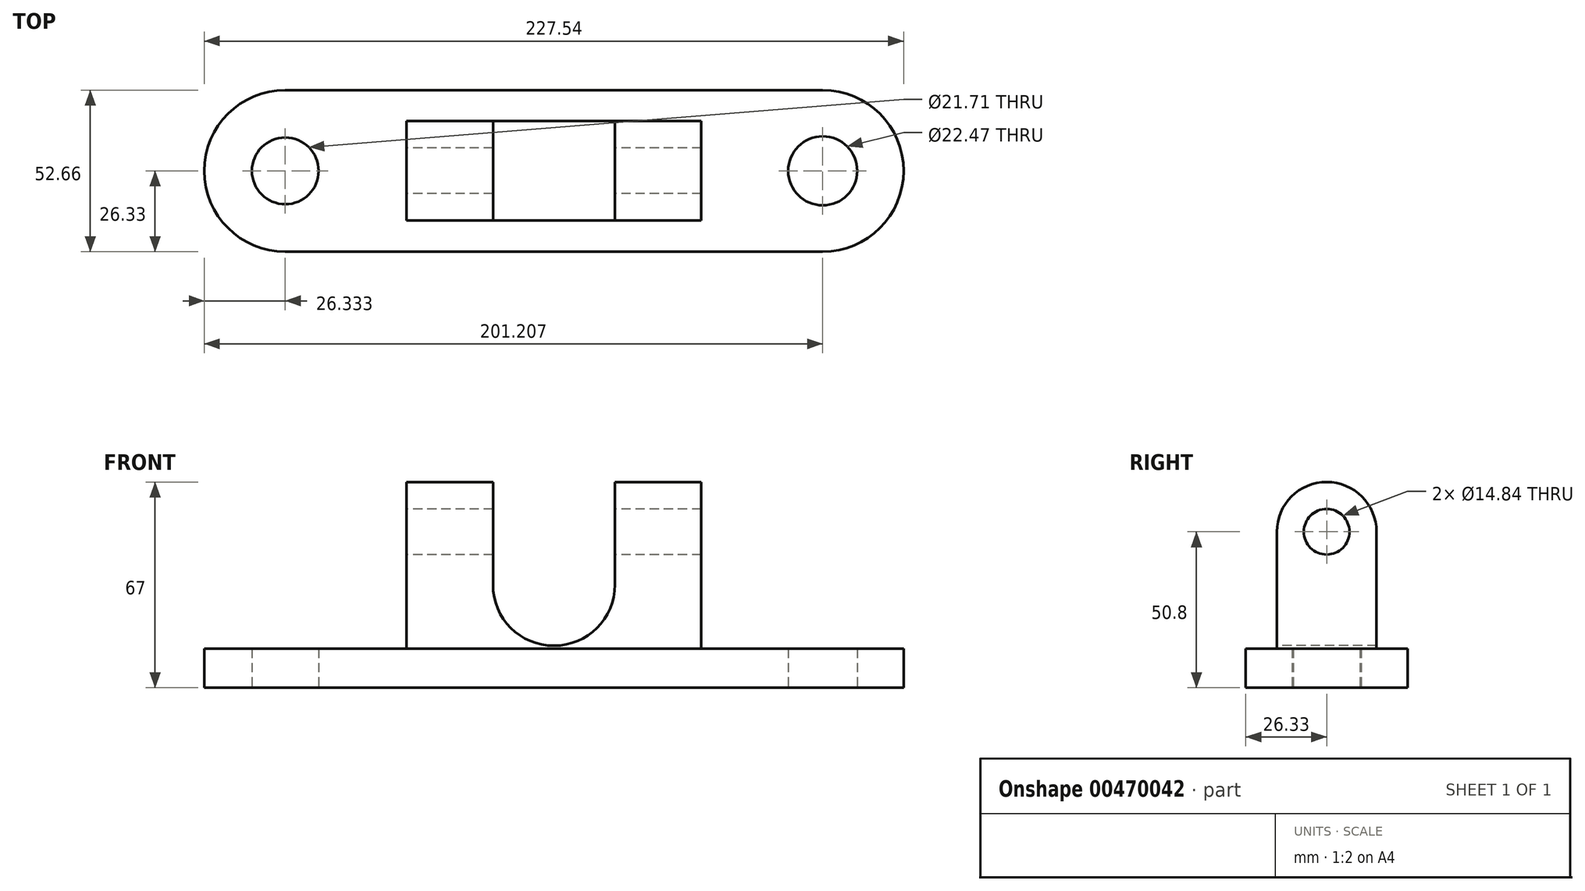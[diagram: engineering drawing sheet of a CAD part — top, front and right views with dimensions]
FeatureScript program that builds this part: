
annotation { "Feature Type Name" : "Feature", "Feature Type Description" : "" }
export const myFeature = defineFeature(function(context is Context, id is Id, definition is map)
    precondition{}
    {
        {
            var Q0;
            Q0=qCreatedBy(makeId("Top.planeOp"),FACE);
            var sketch = newSketch(context, id + "F0", { "sketchPlane" : qUnion([Q0])});
            skLineSegment(sketch, "E0.bottom", {"start": v(87.44, 26.33) * mm, "end": v(-87.44, 26.33) * mm});
            skLineSegment(sketch, "E0.top", {"start": v(87.44, -26.33) * mm, "end": v(-87.44, -26.33) * mm});
            skPoint(sketch, "E0.middle", {"position": v(0, 0) * mm});
            skArc(sketch, "E1", {"start": v(-87.44, 26.33) * mm, "mid": v(-113.77, 0) * mm, "end": v(-87.44, -26.33) * mm});
            skArc(sketch, "E2", {"start": v(87.44, 26.33) * mm, "mid": v(113.77, 0) * mm, "end": v(87.44, -26.33) * mm});
            skCircle(sketch, "E3", {"center": v(-87.44, 0) * mm, "radius": 10.85 * mm});
            skCircle(sketch, "E4", {"center": v(87.44, 0) * mm, "radius": 11.23 * mm});
            skSolve(sketch);
        }
        {
            var Q0;
            Q0=makeQuery(id+"F0.imprint","IMPRINT",FACE,{"disambiguationData":[TD([[makeQuery(id+"F0.imprint","IMPRINT",EDGE,{"derivedFrom":sQuery(id+"F0.wireOp",EDGE,"E0.bottom")}),1.0]])]});
            extrude(context, id + "F1", {"entities" : qUnion([Q0]), "depth" : 12.7 * mm});
        }
        {
            var Q0;
            Q0=makeQuery(id+"F1.opExtrude","CAP_FACE",FACE,{"disambiguationData":[OSD([sQuery(id+"F0.wireOp",EDGE,"E0.bottom"),sQuery(id+"F0.wireOp",EDGE,"E0.top"),sQuery(id+"F0.wireOp",EDGE,"E1"),sQuery(id+"F0.wireOp",EDGE,"E2"),sQuery(id+"F0.wireOp",EDGE,"E3"),sQuery(id+"F0.wireOp",EDGE,"E4")])],"isStart":false});
            var sketch = newSketch(context, id + "F2", { "sketchPlane" : qUnion([Q0])});
            skLineSegment(sketch, "E5.bottom", {"start": v(47.94, 16.2) * mm, "end": v(-47.94, 16.2) * mm});
            skLineSegment(sketch, "E5.top", {"start": v(47.94, -16.2) * mm, "end": v(-47.94, -16.2) * mm});
            skLineSegment(sketch, "E5.left", {"start": v(47.94, 16.2) * mm, "end": v(47.94, -16.2) * mm});
            skLineSegment(sketch, "E5.right", {"start": v(-47.94, 16.2) * mm, "end": v(-47.94, -16.2) * mm});
            skPoint(sketch, "E5.middle", {"position": v(0, 0) * mm});
            skSolve(sketch);
        }
        {
            var Q0;
            Q0=makeQuery(id+"F2.imprint","IMPRINT",FACE,{"disambiguationData":[TD([[makeQuery(id+"F2.imprint","IMPRINT",EDGE,{"derivedFrom":sQuery(id+"F2.wireOp",EDGE,"E5.bottom")}),1.0]])]});
            extrude(context, id + "F3", {"entities" : qUnion([Q0]), "operationType" : NewBodyOperationType.ADD, "depth" : 38.1 * mm});
        }
        {
            var Q0;
            Q0=makeQuery(id+"F3.opExtrude","SWEPT_FACE",FACE,{"disambiguationData":[OSD([sQuery(id+"F2.wireOp",EDGE,"E5.right")])]});
            var sketch = newSketch(context, id + "F4", { "sketchPlane" : qUnion([Q0])});
            skArc(sketch, "E6", {"start": v(16.2, 50.8) * mm, "mid": v(0, 67) * mm, "end": v(-16.2, 50.8) * mm});
            skCircle(sketch, "E7", {"center": v(0, 50.8) * mm, "radius": 7.42 * mm});
            skSolve(sketch);
        }
        {
            var Q0;
            Q0=makeQuery(id+"F4.imprint","IMPRINT",FACE,{"disambiguationData":[TD([[makeQuery(id+"F4.imprint","IMPRINT",EDGE,{"derivedFrom":sQuery(id+"F4.wireOp",EDGE,"E6")}),1.0]])]});
            var Q1;
            Q1=makeQuery(id+"F3.opExtrude","SWEPT_FACE",FACE,{"disambiguationData":[OSD([sQuery(id+"F2.wireOp",EDGE,"E5.left")])]});
            extrude(context, id + "F5", {"entities" : qUnion([Q0]), "operationType" : NewBodyOperationType.ADD, "endBound" : BoundingType.UP_TO_SURFACE, "oppositeDirection" : true, "endBoundEntityFace" : qUnion([Q1]), "depth" : 84.84 * mm});
        }
        {
            var Q0;
            {var subQ0=sQuery(id+"F4.wireOp",EDGE,"E7");var subQ1=makeQuery(id+"F3.opExtrude","CAP_EDGE",EDGE,{"disambiguationData":[OSD([sQuery(id+"F2.wireOp",EDGE,"E5.right")])],"isStart":false});var subQ2=makeQuery(id+"F4.imprint","INTERSECT",VERTEX,{"disambiguationData":[OD(0.0)],"derivedFrom":[subQ1,subQ0]});Q0=makeQuery(id+"F4.imprint","IMPRINT",FACE,{"disambiguationData":[TD([[makeQuery(id+"F4.imprint","IMPRINT",EDGE,{"disambiguationData":[TD([[subQ2,-1.0]])],"derivedFrom":subQ0}),1.0]])]});}
            extrude(context, id + "F6", {"entities" : qUnion([Q0]), "operationType" : NewBodyOperationType.REMOVE, "endBound" : BoundingType.THROUGH_ALL, "oppositeDirection" : true, "depth" : 25.4 * mm});
        }
        {
            var Q0;
            Q0=makeQuery(id+"F3.opExtrude","SWEPT_FACE",FACE,{"disambiguationData":[OSD([sQuery(id+"F2.wireOp",EDGE,"E5.top")])]});
            var sketch = newSketch(context, id + "F7", { "sketchPlane" : qUnion([Q0])});
            skLineSegment(sketch, "E8", {"start": v(0, 12.7) * mm, "end": v(0, 82.86) * mm, "construction": true});
            skPoint(sketch, "E8.endSnap0", {"position": v(0, 50.8) * mm});
            skLineSegment(sketch, "E9.bottom", {"start": v(-19.84, 68.06) * mm, "end": v(19.84, 68.06) * mm});
            skLineSegment(sketch, "E9.left", {"start": v(-19.84, 68.06) * mm, "end": v(-19.84, 33.54) * mm});
            skLineSegment(sketch, "E9.right", {"start": v(19.84, 68.06) * mm, "end": v(19.84, 33.54) * mm});
            skArc(sketch, "E10", {"start": v(19.84, 33.54) * mm, "mid": v(0, 13.7) * mm, "end": v(-19.84, 33.54) * mm});
            skSolve(sketch);
        }
        {
            var Q0;
            Q0 = qSketchRegion(id + "F7", true);
            extrude(context, id + "F8", {"entities" : qUnion([Q0]), "operationType" : NewBodyOperationType.REMOVE, "endBound" : BoundingType.THROUGH_ALL, "oppositeDirection" : true, "depth" : 25.4 * mm});
        }
    });
